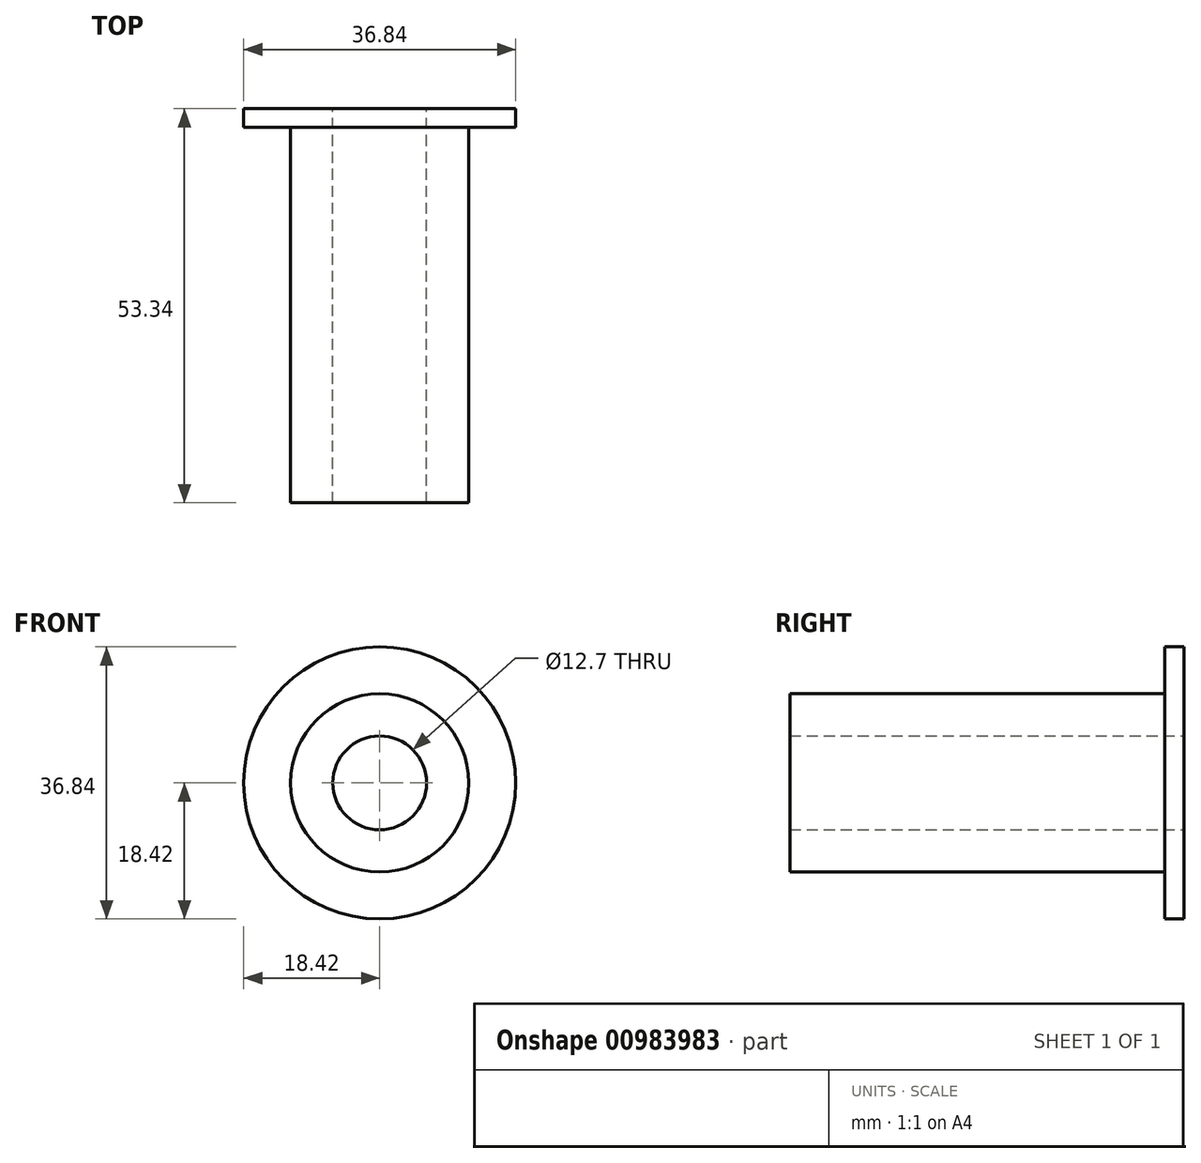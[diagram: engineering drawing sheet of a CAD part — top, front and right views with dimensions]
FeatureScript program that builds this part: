
annotation { "Feature Type Name" : "Feature", "Feature Type Description" : "" }
export const myFeature = defineFeature(function(context is Context, id is Id, definition is map)
    precondition{}
    {
        {
            var Q0;
            Q0=qCreatedBy(makeId("Top.planeOp"),FACE);
            var sketch = newSketch(context, id + "F0", { "sketchPlane" : qUnion([Q0])});
            skLineSegment(sketch, "E0", {"start": v(0, -15.61) * mm, "end": v(12.07, -15.61) * mm});
            skLineSegment(sketch, "E1", {"start": v(12.07, -15.61) * mm, "end": v(12.07, 35.19) * mm});
            skLineSegment(sketch, "E2", {"start": v(12.07, 35.19) * mm, "end": v(18.41, 35.19) * mm});
            skLineSegment(sketch, "E3", {"start": v(18.41, 35.19) * mm, "end": v(18.41, 37.73) * mm});
            skLineSegment(sketch, "E4", {"start": v(18.41, 37.73) * mm, "end": v(0, 37.73) * mm});
            skLineSegment(sketch, "E5", {"start": v(0, 37.73) * mm, "end": v(0, -15.61) * mm});
            skSolve(sketch);
        }
        {
            var Q0;
            Q0=makeQuery(id+"F0.imprint","IMPRINT",FACE,{"disambiguationData":[TD([[makeQuery(id+"F0.imprint","IMPRINT",EDGE,{"derivedFrom":sQuery(id+"F0.wireOp",EDGE,"E0")}),1.0]])]});
            var Q1;
            Q1=sQuery(id+"F0.wireOp",EDGE,"E5");
            revolve(context, id + "F1", {"surfaceOperationType" : NewSurfaceOperationType.NEW, "entities" : qUnion([Q0]), "axis" : qUnion([Q1]), "revolveType" : RevolveType.FULL});
        }
        {
            var Q0;
            Q0=makeQuery(id+"F1.opRevolve","SWEPT_FACE",FACE,{"disambiguationData":[OSD([sQuery(id+"F0.wireOp",EDGE,"E4")])]});
            var sketch = newSketch(context, id + "F2", { "sketchPlane" : qUnion([Q0])});
            skCircle(sketch, "E6", {"center": v(0, 0) * mm, "radius": 6.35 * mm});
            skSolve(sketch);
        }
        {
            var Q0;
            Q0 = qSketchRegion(id + "F2", true);
            extrude(context, id + "F3", {"entities" : qUnion([Q0]), "operationType" : NewBodyOperationType.REMOVE, "oppositeDirection" : true, "depth" : 101.6 * mm, "offsetDistance" : 25.4 * mm});
        }
    });
